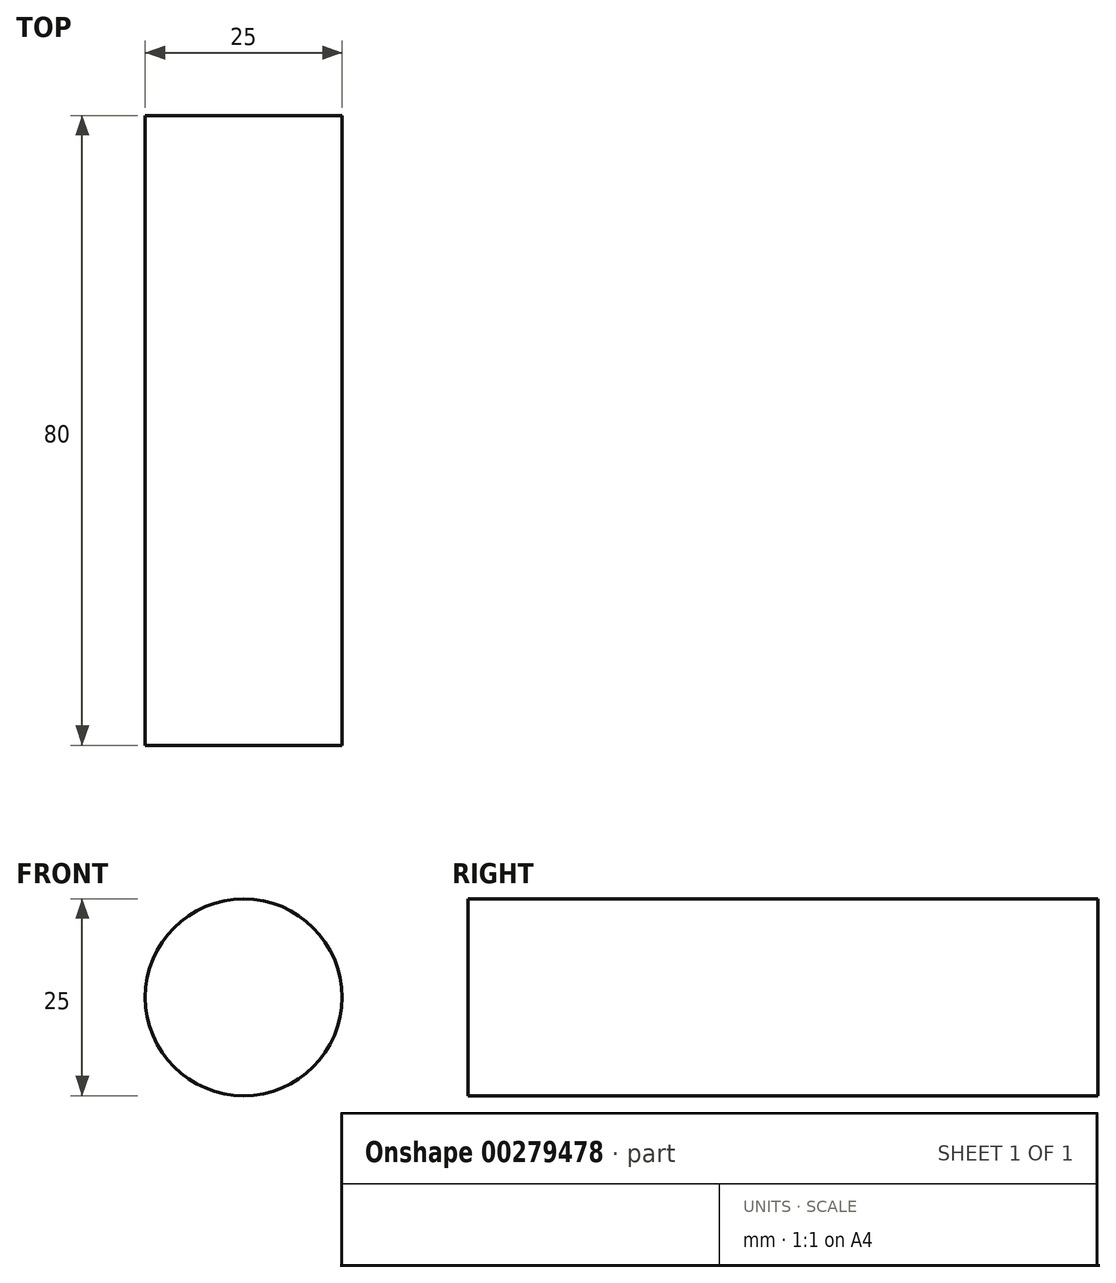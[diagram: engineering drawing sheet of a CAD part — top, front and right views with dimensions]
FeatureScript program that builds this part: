
annotation { "Feature Type Name" : "Feature", "Feature Type Description" : "" }
export const myFeature = defineFeature(function(context is Context, id is Id, definition is map)
    precondition{}
    {
        {
            var Q0;
            Q0=qCreatedBy(makeId("Front.planeOp"),FACE);
            var sketch = newSketch(context, id + "F0", { "sketchPlane" : qUnion([Q0])});
            skCircle(sketch, "E0", {"center": v(0, 0) * mm, "radius": 12.5 * mm});
            skSolve(sketch);
        }
        {
            var Q0;
            Q0=makeQuery(id+"F0.imprint","IMPRINT",FACE,{"disambiguationData":[TD([[makeQuery(id+"F0.imprint","IMPRINT",EDGE,{"derivedFrom":sQuery(id+"F0.wireOp",EDGE,"E0")}),1.0]])]});
            extrude(context, id + "F1", {"entities" : qUnion([Q0]), "depth" : 80 * mm, "offsetDistance" : 25 * mm});
        }
    });
